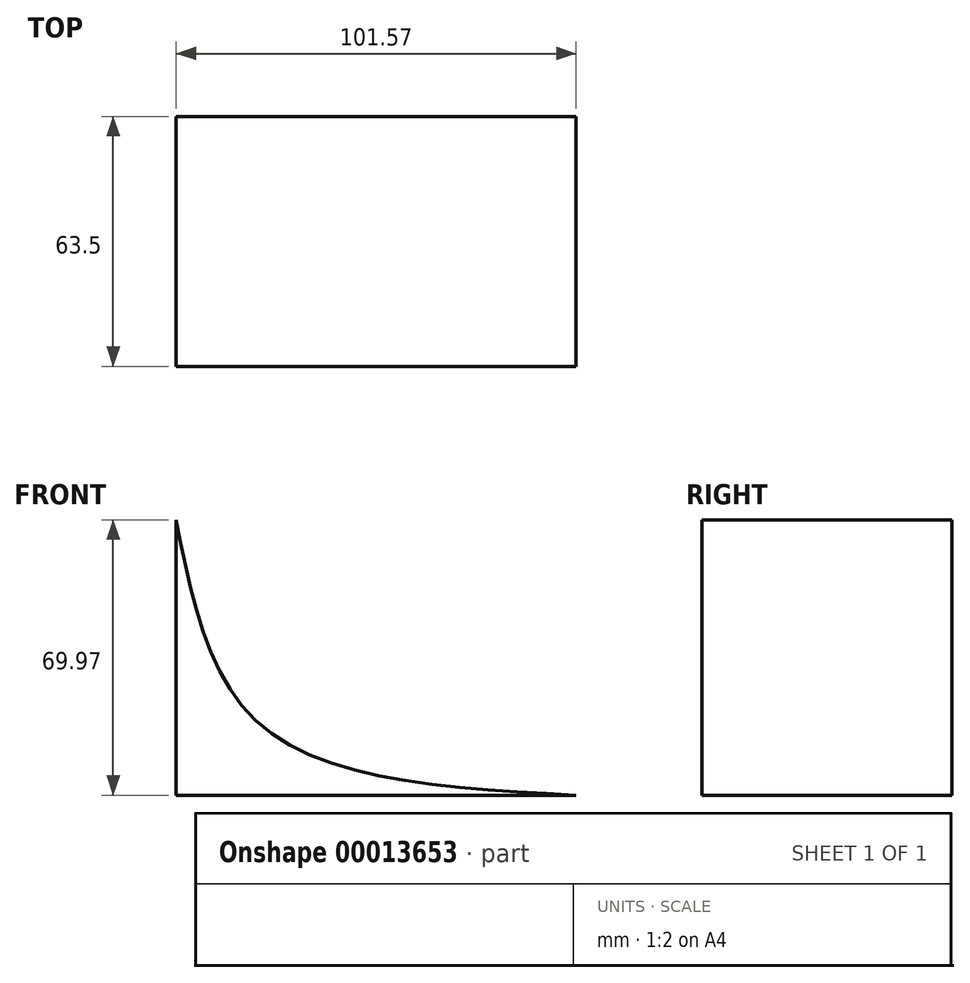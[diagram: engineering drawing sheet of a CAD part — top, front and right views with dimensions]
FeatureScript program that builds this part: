
annotation { "Feature Type Name" : "Feature", "Feature Type Description" : "" }
export const myFeature = defineFeature(function(context is Context, id is Id, definition is map)
    precondition{}
    {
        {
            var Q0;
            Q0=qCreatedBy(makeId("Front.planeOp"),FACE);
            var sketch = newSketch(context, id + "F0", { "sketchPlane" : qUnion([Q0])});
            skLineSegment(sketch, "E0.bottom", {"start": v(0, 0) * mm, "end": v(101.57, 0) * mm});
            skLineSegment(sketch, "E0.top", {"start": v(0, 69.97) * mm, "end": v(101.57, 69.97) * mm});
            skLineSegment(sketch, "E0.left", {"start": v(0, 0) * mm, "end": v(0, 69.97) * mm});
            skLineSegment(sketch, "E0.right", {"start": v(101.57, 0) * mm, "end": v(101.57, 69.97) * mm});
            skSolve(sketch);
        }
        {
            var Q0;
            Q0=makeQuery(id+"F0.imprint","IMPRINT",FACE,{"disambiguationData":[TD([[makeQuery(id+"F0.imprint","IMPRINT",EDGE,{"derivedFrom":sQuery(id+"F0.wireOp",EDGE,"E0.bottom")}),1.0]])]});
            extrude(context, id + "F1", {"entities" : qUnion([Q0]), "depth" : 127 * mm});
        }
        {
            var Q0;
            Q0=makeQuery(id+"F1.opExtrude","CAP_FACE",FACE,{"disambiguationData":[OSD([sQuery(id+"F0.wireOp",EDGE,"E0.bottom"),sQuery(id+"F0.wireOp",EDGE,"E0.top"),sQuery(id+"F0.wireOp",EDGE,"E0.left"),sQuery(id+"F0.wireOp",EDGE,"E0.right")])],"isStart":false});
            var sketch = newSketch(context, id + "F2", { "sketchPlane" : qUnion([Q0])});
            skFitSpline(sketch, "E1", {"points": [v(0, 69.97) * mm, v(22.07, 17.3) * mm, v(101.57, 0) * mm], "startDerivative": vector(26.14, -134.63) * mm, "endDerivative": vector(172.7, -9) * mm});
            skSolve(sketch);
        }
        {
            var Q0;
            Q0=makeQuery(id+"F2.imprint","IMPRINT",FACE,{"disambiguationData":[TD([[makeQuery(id+"F2.imprint","IMPRINT",EDGE,{"derivedFrom":sQuery(id+"F2.wireOp",EDGE,"E1")}),-1.0]])]});
            extrude(context, id + "F3", {"entities" : qUnion([Q0]), "operationType" : NewBodyOperationType.INTERSECT, "oppositeDirection" : true, "depth" : 63.5 * mm});
        }
    });
